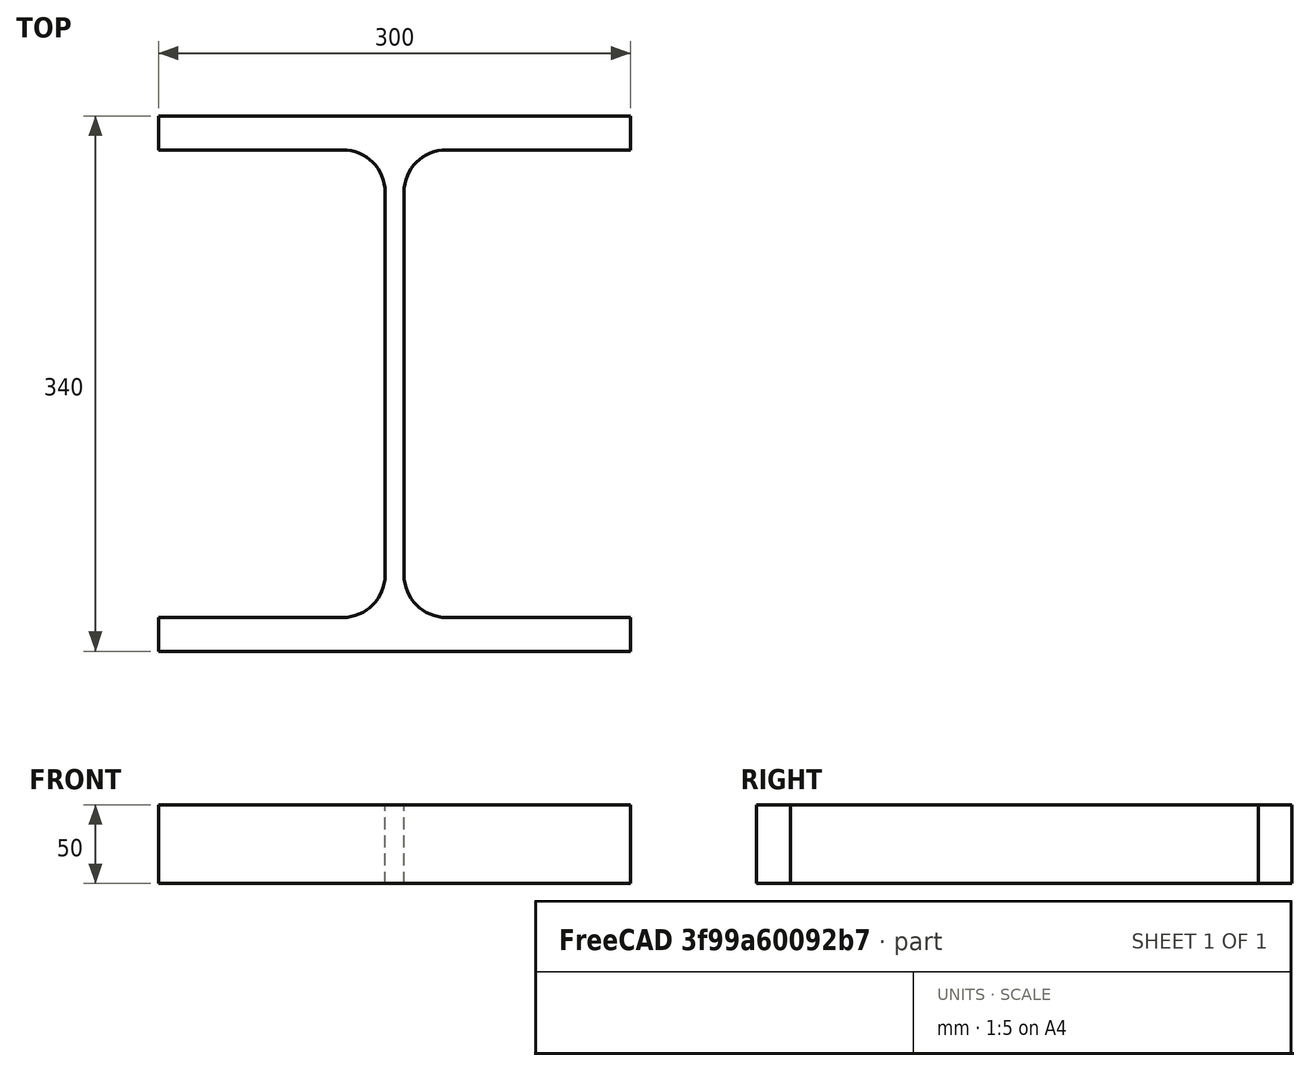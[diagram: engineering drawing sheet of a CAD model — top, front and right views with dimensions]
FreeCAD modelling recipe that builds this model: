
FCSTD DOCUMENT  (FreeCAD 0.15R4671 (Git))
Label: HE-B-Profile 340 DIN1025-2 S235JR
License: All rights reserved
LicenseURL: http://en.wikipedia.org/wiki/All_rights_reserved
objects: Sketcher::SketchObject×1, Part::Extrusion×1
note: 2 computed .brp shape members not serialized (recipe doc carries the construction recipe); baked Part::Feature solids carry a one-line shape summary decoded from their .brp

FEATURE [Sketcher::SketchObject] Sketch
  sketch-geometry (16):
    g0: LineSegment StartX=6 StartY=-121.5 StartZ=0 EndX=6 EndY=121.5 EndZ=0
    g1: LineSegment StartX=33 StartY=148.5 StartZ=0 EndX=150 EndY=148.5 EndZ=0
    g2: LineSegment StartX=150 StartY=148.5 StartZ=0 EndX=150 EndY=170 EndZ=0
    g3: LineSegment StartX=150 StartY=170 StartZ=0 EndX=-150 EndY=170 EndZ=0
    g4: LineSegment StartX=-150 StartY=170 StartZ=0 EndX=-150 EndY=148.5 EndZ=0
    g5: LineSegment StartX=-150 StartY=148.5 StartZ=0 EndX=-33 EndY=148.5 EndZ=0
    g6: LineSegment StartX=-6 StartY=121.5 StartZ=0 EndX=-6 EndY=-121.5 EndZ=0
    g7: LineSegment StartX=-33 StartY=-148.5 StartZ=0 EndX=-150 EndY=-148.5 EndZ=0
    g8: LineSegment StartX=-150 StartY=-148.5 StartZ=0 EndX=-150 EndY=-170 EndZ=0
    g9: LineSegment StartX=-150 StartY=-170 StartZ=0 EndX=150 EndY=-170 EndZ=0
    g10: LineSegment StartX=150 StartY=-170 StartZ=0 EndX=150 EndY=-148.5 EndZ=0
    g11: LineSegment StartX=150 StartY=-148.5 StartZ=0 EndX=33 EndY=-148.5 EndZ=0
    g12: ArcOfCircle CenterX=33 CenterY=121.5 CenterZ=0 NormalX=0 NormalY=0 NormalZ=1 Radius=27 StartAngle=1.5708 EndAngle=3.14159
    g13: ArcOfCircle CenterX=33 CenterY=-121.5 CenterZ=0 NormalX=0 NormalY=0 NormalZ=1 Radius=27 StartAngle=3.14159 EndAngle=4.71239
    g14: ArcOfCircle CenterX=-33 CenterY=121.5 CenterZ=0 NormalX=0 NormalY=0 NormalZ=1 Radius=27 StartAngle=0 EndAngle=1.5708
    g15: ArcOfCircle CenterX=-33 CenterY=-121.5 CenterZ=0 NormalX=0 NormalY=0 NormalZ=1 Radius=27 StartAngle=4.71239 EndAngle=6.28319
  constraints (42):
    c: Vertical(g0)
    c: Coincident(g2,g1)
    c: Vertical(g2)
    c: Coincident(g3,g2)
    c: Coincident(g4,g3)
    c: Vertical(g4)
    c: Coincident(g5,g4)
    c: Horizontal(g5)
    c: Vertical(g6)
    c: Horizontal(g7)
    c: Coincident(g8,g7)
    c: Vertical(g8)
    c: Coincident(g9,g8)
    c: Horizontal(g9)
    c: Coincident(g10,g9)
    c: Vertical(g10)
    c: Coincident(g11,g10)
    c: Horizontal(g11)
    c: Tangent(g1,g12) = 1.5708
    c: Tangent(g0,g12) = 1.5708
    c: Tangent(g0,g13) = 1.5708
    c: Tangent(g11,g13) = 1.5708
    c: Tangent(g5,g14) = 1.5708
    c: Tangent(g6,g14) = 1.5708
    c: Tangent(g6,g15) = 1.5708
    c: Tangent(g7,g15) = 1.5708
    c: Equal(g3,g9)
    c: Equal(g2,g4)
    c: Equal(g4,g8)
    c: Equal(g8,g10)
    c: Equal(g12,g14)
    c: Equal(g14,g15)
    c: Equal(g15,g13)
    c: Symmetric(g2,g3,g-2)
    c: Symmetric(g9,g8,g-2)
    c: Symmetric(g0,g6,g-2)
    c: Symmetric(g2,g9,g-1)
    c: DistanceY(g2,g9) = -340
    c: DistanceX(g3) = -300
    c: DistanceX(g0,g6) = -12
    c: DistanceY(g2) = 21.5
    c: Radius(g12) = 27
FEATURE [Part::Extrusion] Extrude  label="HE-B-Profile 340 DIN1025-2 S235JR"
  Base = -> Sketch
  Dir = (0,0,50)
  Solid = true
